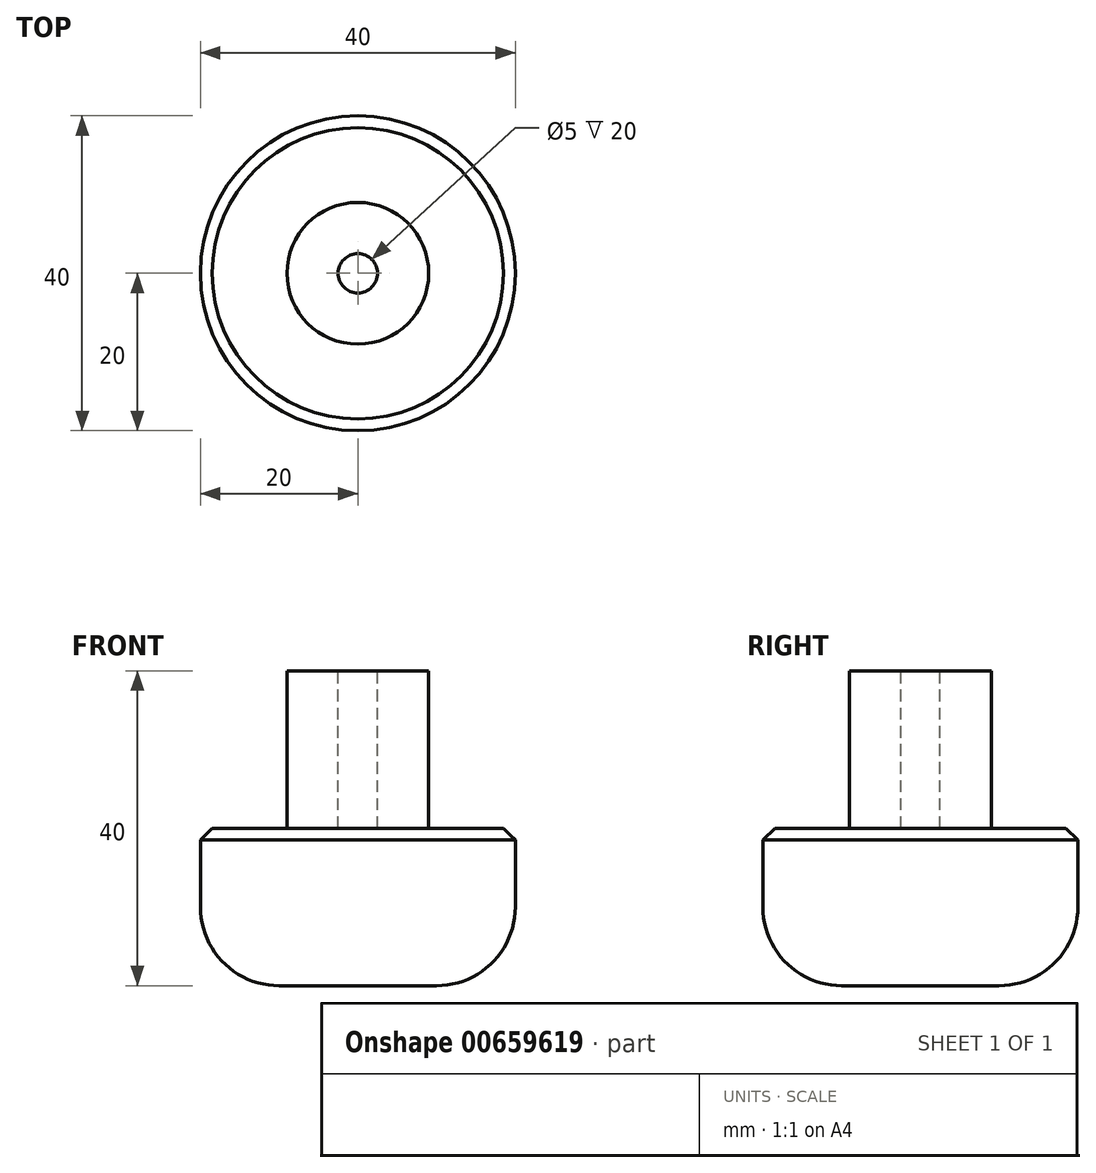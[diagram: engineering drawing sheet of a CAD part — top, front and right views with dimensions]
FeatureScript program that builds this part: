
annotation { "Feature Type Name" : "Feature", "Feature Type Description" : "" }
export const myFeature = defineFeature(function(context is Context, id is Id, definition is map)
    precondition{}
    {
        {
            var Q0;
            Q0=qCreatedBy(makeId("Top.planeOp"),FACE);
            var sketch = newSketch(context, id + "F0", { "sketchPlane" : qUnion([Q0])});
            skCircle(sketch, "E0", {"center": v(0, 0) * mm, "radius": 20 * mm});
            skSolve(sketch);
        }
        {
            var Q0;
            Q0 = qSketchRegion(id + "F0", true);
            extrude(context, id + "F1", {"entities" : qUnion([Q0]), "depth" : 20 * mm, "offsetDistance" : 25 * mm});
        }
        {
            var Q0;
            Q0=makeQuery(id+"F1.opExtrude","CAP_EDGE",EDGE,{"disambiguationData":[OSD([sQuery(id+"F0.wireOp",EDGE,"E0")])],"isStart":true});
            fillet(context, id + "F2", {"entities" : qUnion([Q0]), "radius" : 10 * mm, "tangentPropagation" : true, "allowEdgeOverflow" : false});
        }
        {
            var Q0;
            Q0=makeQuery(id+"F1.opExtrude","CAP_FACE",FACE,{"disambiguationData":[OSD([sQuery(id+"F0.wireOp",EDGE,"E0")])],"isStart":false});
            var sketch = newSketch(context, id + "F3", { "sketchPlane" : qUnion([Q0])});
            skCircle(sketch, "E1", {"center": v(0, 0) * mm, "radius": 9 * mm});
            skSolve(sketch);
        }
        {
            var Q0;
            Q0=makeQuery(id+"F3.imprint","IMPRINT",FACE,{"disambiguationData":[TD([[makeQuery(id+"F3.imprint","IMPRINT",EDGE,{"derivedFrom":sQuery(id+"F3.wireOp",EDGE,"E1")}),1.0]])]});
            extrude(context, id + "F4", {"entities" : qUnion([Q0]), "operationType" : NewBodyOperationType.ADD, "depth" : 20 * mm, "offsetDistance" : 25 * mm});
        }
        {
            var Q0;
            Q0=makeQuery(id+"F4.opExtrude","CAP_FACE",FACE,{"disambiguationData":[OSD([sQuery(id+"F3.wireOp",EDGE,"E1")])],"isStart":false});
            var sketch = newSketch(context, id + "F5", { "sketchPlane" : qUnion([Q0])});
            skCircle(sketch, "E2", {"center": v(0, 0) * mm, "radius": 2.5 * mm});
            skSolve(sketch);
        }
        {
            var Q0;
            Q0=makeQuery(id+"F5.imprint","IMPRINT",FACE,{"disambiguationData":[TD([[makeQuery(id+"F5.imprint","IMPRINT",EDGE,{"derivedFrom":sQuery(id+"F5.wireOp",EDGE,"E2")}),1.0]])]});
            extrude(context, id + "F6", {"entities" : qUnion([Q0]), "operationType" : NewBodyOperationType.REMOVE, "oppositeDirection" : true, "depth" : 20 * mm, "offsetDistance" : 25 * mm});
        }
        {
            var Q0;
            Q0=makeQuery(id+"F1.opExtrude","CAP_EDGE",EDGE,{"disambiguationData":[OSD([sQuery(id+"F0.wireOp",EDGE,"E0")])],"isStart":false});
            chamfer(context, id + "F7", {"entities" : qUnion([Q0]), "width" : 1.5 * mm, "tangentPropagation" : true});
        }
    });
